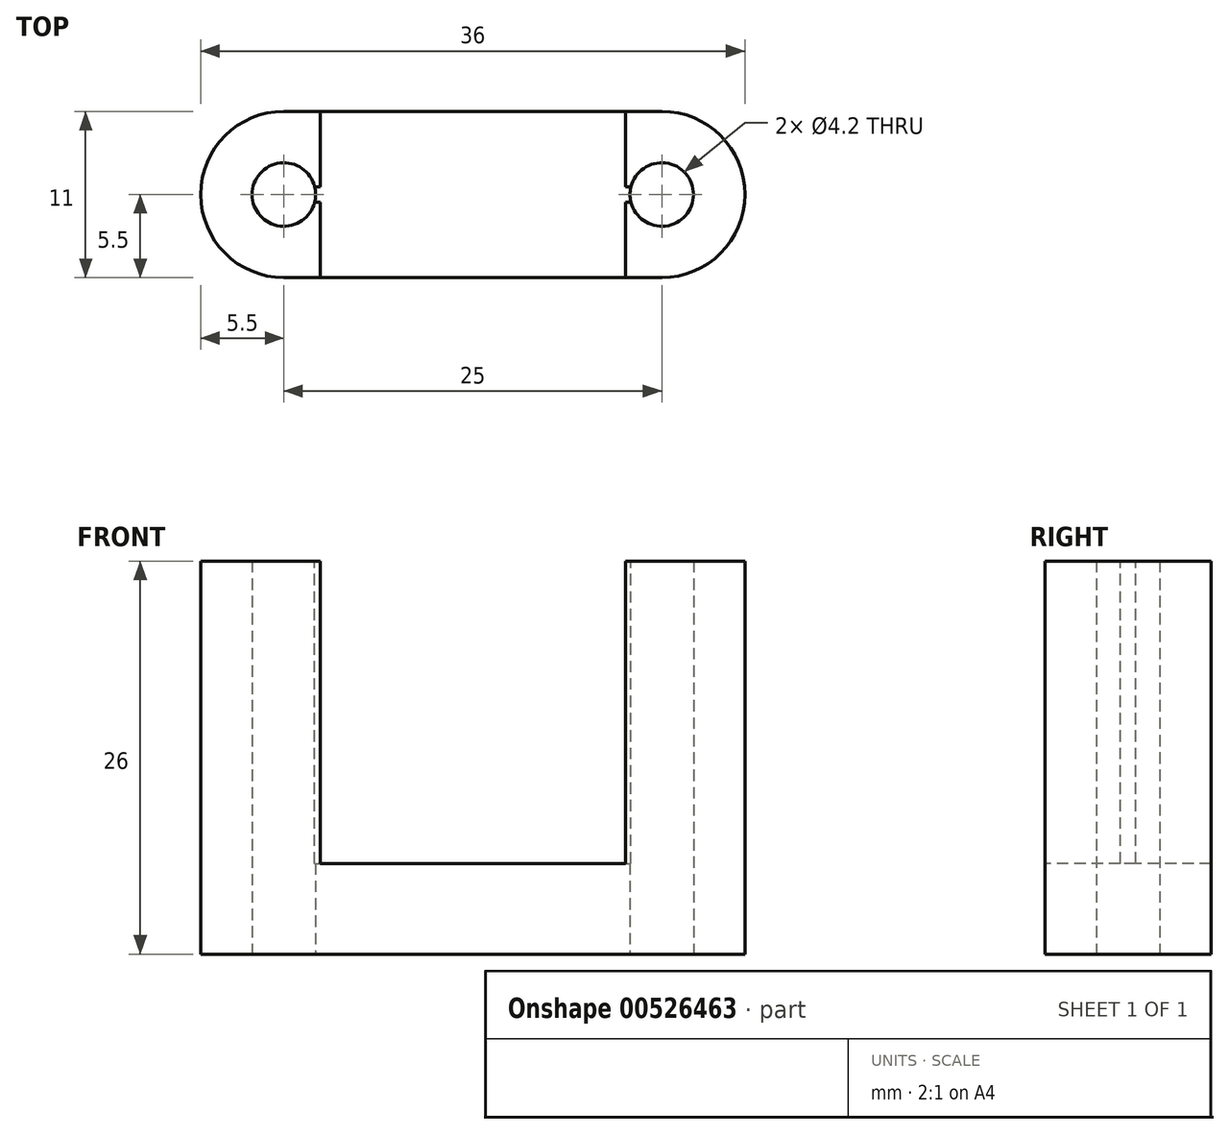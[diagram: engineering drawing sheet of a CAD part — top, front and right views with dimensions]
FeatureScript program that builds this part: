
annotation { "Feature Type Name" : "Feature", "Feature Type Description" : "" }
export const myFeature = defineFeature(function(context is Context, id is Id, definition is map)
    precondition{}
    {
        {
            var Q0;
            Q0=qCreatedBy(makeId("Top.planeOp"),FACE);
            var sketch = newSketch(context, id + "F0", { "sketchPlane" : qUnion([Q0])});
            skLineSegment(sketch, "E0", {"start": v(-12.5, 0) * mm, "end": v(12.5, 0) * mm, "construction": true});
            skArc(sketch, "E1.0.startCap", {"start": v(-12.5, -5.5) * mm, "mid": v(-18, 0) * mm, "end": v(-12.5, 5.5) * mm});
            skArc(sketch, "E1.0.endCap", {"start": v(12.5, 5.5) * mm, "mid": v(18, 0) * mm, "end": v(12.5, -5.5) * mm});
            skLineSegment(sketch, "E1.0.left", {"start": v(-12.5, 5.5) * mm, "end": v(12.5, 5.5) * mm});
            skLineSegment(sketch, "E1.0.right", {"start": v(-12.5, -5.5) * mm, "end": v(12.5, -5.5) * mm});
            skCircle(sketch, "E2", {"center": v(-12.5, 0) * mm, "radius": 2.1 * mm});
            skCircle(sketch, "E3", {"center": v(12.5, 0) * mm, "radius": 2.1 * mm});
            skSolve(sketch);
        }
        {
            var Q0;
            Q0 = qSketchRegion(id + "F0", true);
            extrude(context, id + "F1", {"entities" : qUnion([Q0]), "depth" : 26 * mm, "offsetDistance" : 25 * mm});
        }
        {
            var Q0;
            Q0=makeQuery(id+"F1.opExtrude","CAP_FACE",FACE,{"disambiguationData":[OSD([sQuery(id+"F0.wireOp",EDGE,"E1.0.startCap"),sQuery(id+"F0.wireOp",EDGE,"E1.0.endCap"),sQuery(id+"F0.wireOp",EDGE,"E1.0.left"),sQuery(id+"F0.wireOp",EDGE,"E1.0.right"),sQuery(id+"F0.wireOp",EDGE,"E2"),sQuery(id+"F0.wireOp",EDGE,"E3")])],"isStart":false});
            var sketch = newSketch(context, id + "F2", { "sketchPlane" : qUnion([Q0])});
            skLineSegment(sketch, "E4.bottom", {"start": v(-10.1, 5.5) * mm, "end": v(10.1, 5.5) * mm});
            skLineSegment(sketch, "E4.top", {"start": v(-10.1, -5.5) * mm, "end": v(10.1, -5.5) * mm});
            skLineSegment(sketch, "E4.left", {"start": v(-10.1, 5.5) * mm, "end": v(-10.1, 0.5) * mm});
            skLineSegment(sketch, "E4.right", {"start": v(10.1, 5.5) * mm, "end": v(10.1, 0.5) * mm});
            skLineSegment(sketch, "E5.bottom", {"start": v(-10.46, 0.5) * mm, "end": v(-10.1, 0.5) * mm});
            skLineSegment(sketch, "E5.top", {"start": v(-10.46, -0.5) * mm, "end": v(-10.1, -0.5) * mm});
            skLineSegment(sketch, "E5.left", {"start": v(-10.46, 0.5) * mm, "end": v(-10.46, -0.5) * mm});
            skLineSegment(sketch, "E6.bottom", {"start": v(10.1, 0.5) * mm, "end": v(10.46, 0.5) * mm});
            skLineSegment(sketch, "E6.top", {"start": v(10.1, -0.5) * mm, "end": v(10.46, -0.5) * mm});
            skLineSegment(sketch, "E6.right", {"start": v(10.46, 0.5) * mm, "end": v(10.46, -0.5) * mm});
            skLineSegment(sketch, "E7", {"start": v(-10.1, 5.5) * mm, "end": v(10.1, -5.5) * mm, "construction": true});
            skLineSegment(sketch, "E8", {"start": v(0, 0) * mm, "end": v(-10.46, 0) * mm, "construction": true});
            skLineSegment(sketch, "E9.trimOffspring", {"start": v(-10.1, -0.5) * mm, "end": v(-10.1, -5.5) * mm});
            skLineSegment(sketch, "E10.trimOffspring", {"start": v(10.1, -0.5) * mm, "end": v(10.1, -5.5) * mm});
            skSolve(sketch);
        }
        {
            var Q0;
            Q0 = qSketchRegion(id + "F2", true);
            extrude(context, id + "F3", {"entities" : qUnion([Q0]), "operationType" : NewBodyOperationType.REMOVE, "oppositeDirection" : true, "depth" : 20 * mm, "offsetDistance" : 25 * mm});
        }
    });
